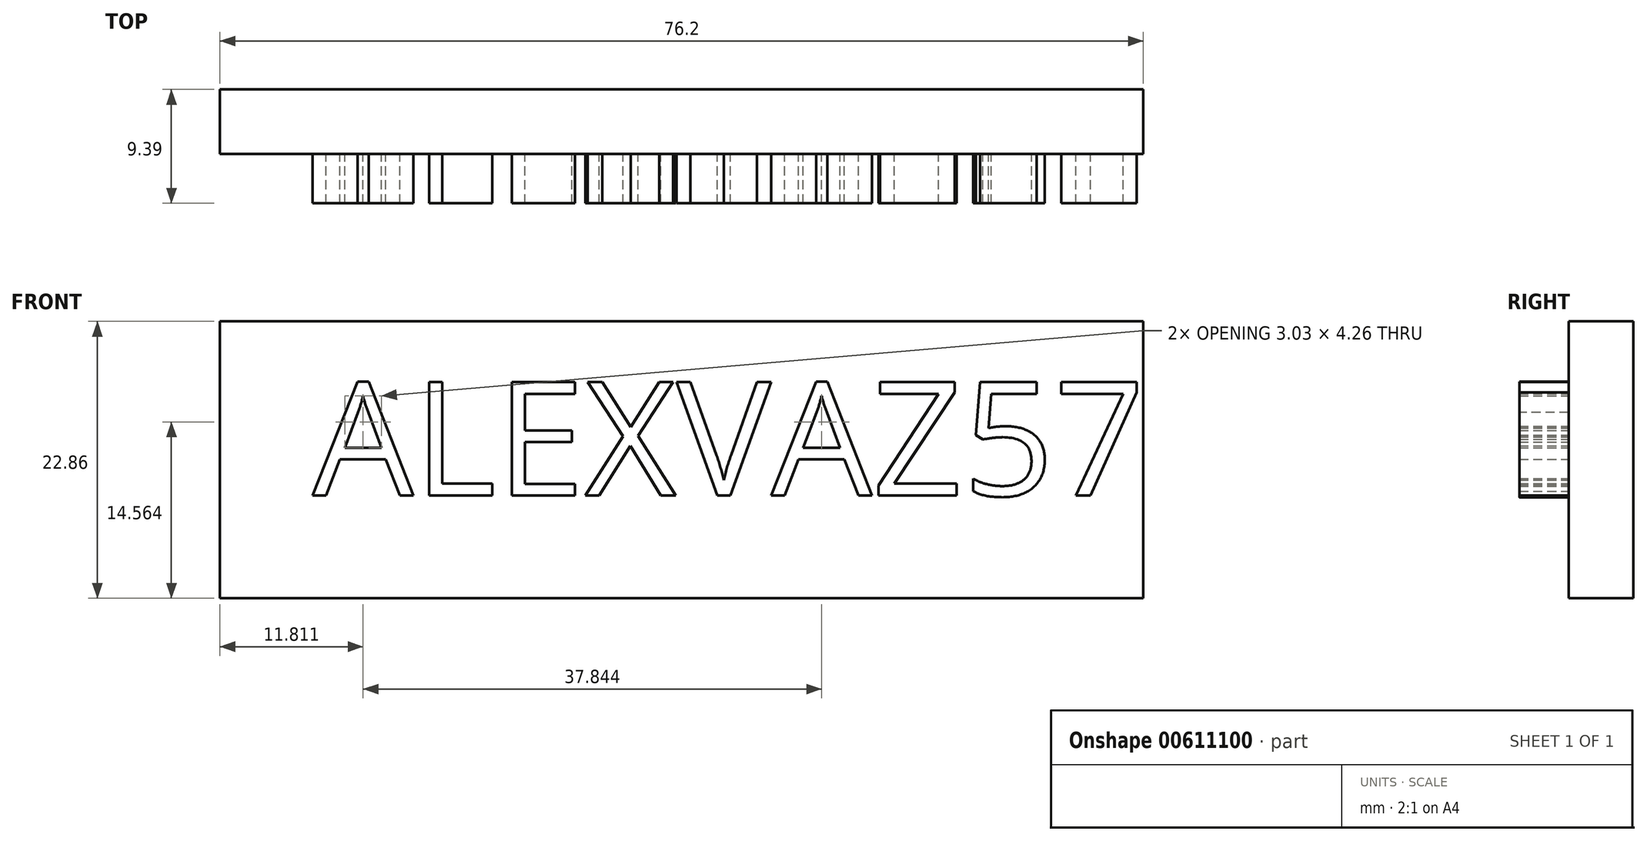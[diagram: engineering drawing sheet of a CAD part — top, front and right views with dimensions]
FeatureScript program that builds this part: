
annotation { "Feature Type Name" : "Feature", "Feature Type Description" : "" }
export const myFeature = defineFeature(function(context is Context, id is Id, definition is map)
    precondition{}
    {
        {
            var Q0;
            Q0=qCreatedBy(makeId("Front.planeOp"),FACE);
            var sketch = newSketch(context, id + "F0", { "sketchPlane" : qUnion([Q0])});
            skLineSegment(sketch, "E0.bottom", {"start": v(-42.08, 22.86) * mm, "end": v(34.12, 22.86) * mm});
            skLineSegment(sketch, "E0.top", {"start": v(-42.08, 0) * mm, "end": v(34.12, 0) * mm});
            skLineSegment(sketch, "E0.left", {"start": v(-42.08, 22.86) * mm, "end": v(-42.08, 0) * mm});
            skLineSegment(sketch, "E0.right", {"start": v(34.12, 22.86) * mm, "end": v(34.12, 0) * mm});
            skSolve(sketch);
        }
        {
            var Q0;
            Q0=makeQuery(id+"F0.imprint","IMPRINT",FACE,{"disambiguationData":[TD([[makeQuery(id+"F0.imprint","IMPRINT",EDGE,{"derivedFrom":sQuery(id+"F0.wireOp",EDGE,"E0.bottom")}),-1.0]])]});
            var sketch = newSketch(context, id + "F1", { "sketchPlane" : qUnion([Q0])});
            skText(sketch, "E1", { "text": "ALEXVAZ57\n", "fontName": "OpenSans-Regular.ttf"});
            const initialGuessF1  = {"E1": [-0.03443, 0.00847, 1, 0, 0.00946]};
            skSetInitialGuess(sketch, initialGuessF1);
            skSolve(sketch);
        }
        {
            var Q0;
            Q0 = qSketchRegion(id + "F1", true);
            extrude(context, id + "F2", {"entities" : qUnion([Q0]), "depth" : 4.06 * mm, "offsetDistance" : 25.4 * mm});
        }
        {
            var Q0;
            Q0=makeQuery(id+"F0.imprint","IMPRINT",FACE,{"disambiguationData":[TD([[makeQuery(id+"F0.imprint","IMPRINT",EDGE,{"derivedFrom":sQuery(id+"F0.wireOp",EDGE,"E0.bottom")}),-1.0]])]});
            extrude(context, id + "F3", {"entities" : qUnion([Q0]), "oppositeDirection" : true, "depth" : 5.33 * mm, "offsetDistance" : 25.4 * mm});
        }
    });
